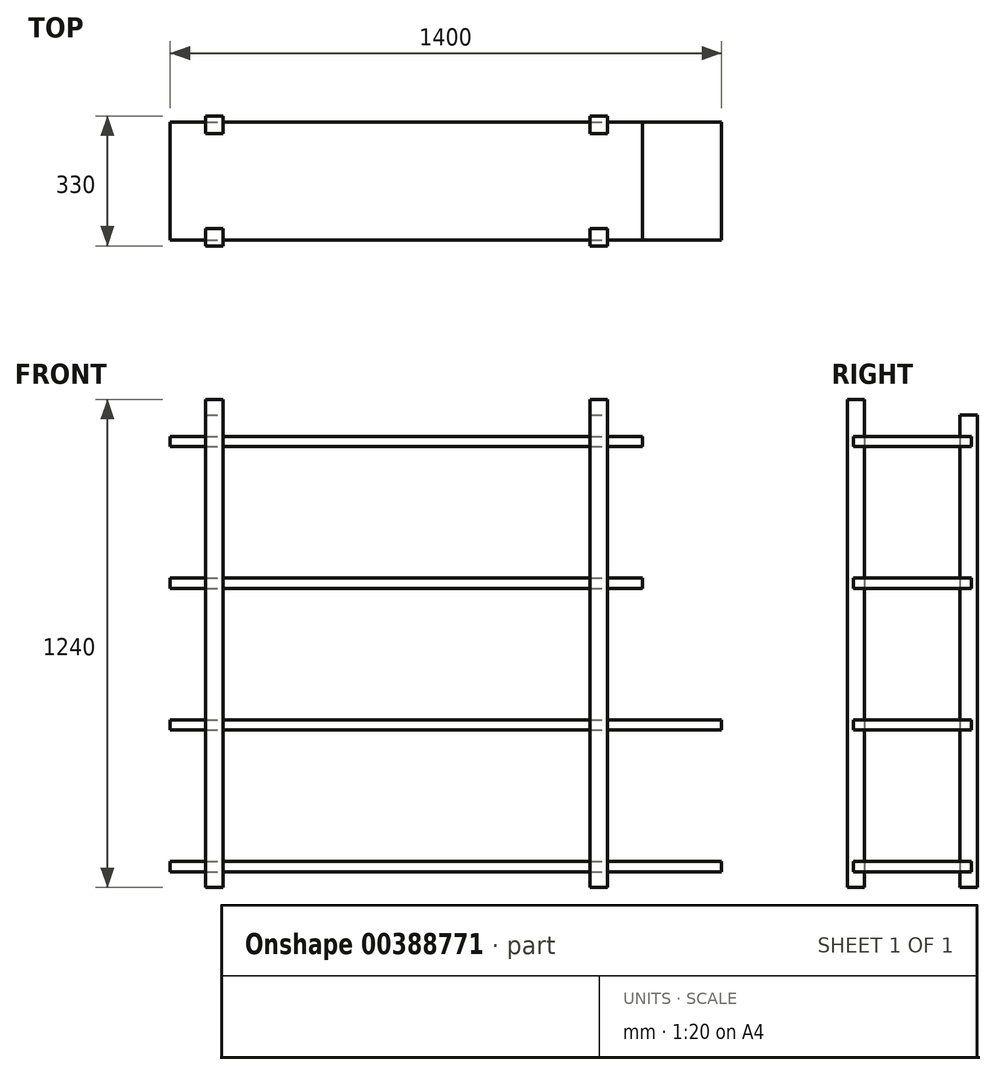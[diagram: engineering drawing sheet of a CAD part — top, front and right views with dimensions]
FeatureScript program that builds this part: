
annotation { "Feature Type Name" : "Feature", "Feature Type Description" : "" }
export const myFeature = defineFeature(function(context is Context, id is Id, definition is map)
    precondition{}
    {
        {
            var Q0;
            Q0=qCreatedBy(makeId("Front.planeOp"),FACE);
            var sketch = newSketch(context, id + "F0", { "sketchPlane" : qUnion([Q0])});
            skLineSegment(sketch, "E0.bottom", {"start": v(-700, 26) * mm, "end": v(700, 26) * mm});
            skLineSegment(sketch, "E0.top", {"start": v(-700, 0) * mm, "end": v(700, 0) * mm});
            skLineSegment(sketch, "E0.left", {"start": v(-700, 26) * mm, "end": v(-700, 0) * mm});
            skLineSegment(sketch, "E0.right", {"start": v(700, 26) * mm, "end": v(700, 0) * mm});
            skSolve(sketch);
        }
        {
            var Q0;
            Q0=qCreatedBy(makeId("Front.planeOp"),FACE);
            var sketch = newSketch(context, id + "F1", { "sketchPlane" : qUnion([Q0])});
            skLineSegment(sketch, "E1.bottom", {"start": v(-700, 386) * mm, "end": v(700, 386) * mm});
            skLineSegment(sketch, "E1.top", {"start": v(-700, 360) * mm, "end": v(700, 360) * mm});
            skLineSegment(sketch, "E1.left", {"start": v(-700, 386) * mm, "end": v(-700, 360) * mm});
            skLineSegment(sketch, "E1.right", {"start": v(700, 386) * mm, "end": v(700, 360) * mm});
            skSolve(sketch);
        }
        {
            var Q0;
            Q0=qCreatedBy(makeId("Front.planeOp"),FACE);
            var sketch = newSketch(context, id + "F2", { "sketchPlane" : qUnion([Q0])});
            skLineSegment(sketch, "E2.bottom", {"start": v(-700, 746) * mm, "end": v(500, 746) * mm});
            skLineSegment(sketch, "E2.top", {"start": v(-700, 720) * mm, "end": v(500, 720) * mm});
            skLineSegment(sketch, "E2.left", {"start": v(-700, 746) * mm, "end": v(-700, 720) * mm});
            skLineSegment(sketch, "E2.right", {"start": v(500, 746) * mm, "end": v(500, 720) * mm});
            skSolve(sketch);
        }
        {
            var Q0;
            Q0=qCreatedBy(makeId("Front.planeOp"),FACE);
            var sketch = newSketch(context, id + "F3", { "sketchPlane" : qUnion([Q0])});
            skLineSegment(sketch, "E3.bottom", {"start": v(-700, 1106) * mm, "end": v(500, 1106) * mm});
            skLineSegment(sketch, "E3.top", {"start": v(-700, 1080) * mm, "end": v(500, 1080) * mm});
            skLineSegment(sketch, "E3.left", {"start": v(-700, 1106) * mm, "end": v(-700, 1080) * mm});
            skLineSegment(sketch, "E3.right", {"start": v(500, 1106) * mm, "end": v(500, 1080) * mm});
            skSolve(sketch);
        }
        {
            var Q0;
            Q0=qCreatedBy(makeId("Front.planeOp"),FACE);
            var sketch = newSketch(context, id + "F4", { "sketchPlane" : qUnion([Q0])});
            skLineSegment(sketch, "E4.bottom", {"start": v(-610, 1160) * mm, "end": v(-566, 1160) * mm});
            skLineSegment(sketch, "E4.top", {"start": v(-610, -40) * mm, "end": v(-566, -40) * mm});
            skLineSegment(sketch, "E4.left", {"start": v(-610, 1160) * mm, "end": v(-610, -40) * mm});
            skLineSegment(sketch, "E4.right", {"start": v(-566, 1160) * mm, "end": v(-566, -40) * mm});
            skSolve(sketch);
        }
        {
            var Q0;
            Q0=qCreatedBy(makeId("Front.planeOp"),FACE);
            var sketch = newSketch(context, id + "F5", { "sketchPlane" : qUnion([Q0])});
            skLineSegment(sketch, "E5.bottom", {"start": v(366, 1160) * mm, "end": v(410, 1160) * mm});
            skLineSegment(sketch, "E5.top", {"start": v(366, -40) * mm, "end": v(410, -40) * mm});
            skLineSegment(sketch, "E5.left", {"start": v(366, 1160) * mm, "end": v(366, -40) * mm});
            skLineSegment(sketch, "E5.right", {"start": v(410, 1160) * mm, "end": v(410, -40) * mm});
            skSolve(sketch);
        }
        {
            var Q0;
            Q0=qSketchRegion(id+"F0",true);
            extrude(context, id + "F6", {"entities" : qUnion([Q0]), "depth" : 300 * mm});
        }
        {
            var Q0;
            Q0=qSketchRegion(id+"F1",true);
            var Q1;
            Q1=makeQuery(id+"F2.imprint","IMPRINT",FACE,{"disambiguationData":[TD([[makeQuery(id+"F2.imprint","IMPRINT",EDGE,{"derivedFrom":sQuery(id+"F2.wireOp",EDGE,"E2.bottom")}),-1.0]])]});
            var Q2;
            Q2=makeQuery(id+"F3.imprint","IMPRINT",FACE,{"disambiguationData":[TD([[makeQuery(id+"F3.imprint","IMPRINT",EDGE,{"derivedFrom":sQuery(id+"F3.wireOp",EDGE,"E3.bottom")}),-1.0]])]});
            extrude(context, id + "F7", {"entities" : qUnion([Q0, Q1, Q2]), "depth" : 300 * mm});
        }
        {
            var Q0;
            Q0=qCreatedBy(makeId("Top.planeOp"),FACE);
            var sketch = newSketch(context, id + "F8", { "sketchPlane" : qUnion([Q0])});
            skLineSegment(sketch, "E6.bottom", {"start": v(-610, -271) * mm, "end": v(-566, -271) * mm});
            skLineSegment(sketch, "E6.top", {"start": v(-610, -315) * mm, "end": v(-566, -315) * mm});
            skLineSegment(sketch, "E6.left", {"start": v(-610, -271) * mm, "end": v(-610, -315) * mm});
            skLineSegment(sketch, "E6.right", {"start": v(-566, -271) * mm, "end": v(-566, -315) * mm});
            skSolve(sketch);
        }
        {
            var Q0;
            Q0=qSketchRegion(id+"F8",true);
            extrude(context, id + "F9", {"entities" : qUnion([Q0]), "depth" : 1200 * mm, "hasSecondDirection" : true, "secondDirectionOppositeDirection" : true, "secondDirectionDepth" : 40 * mm});
        }
        {
            var Q0;
            Q0=qCreatedBy(makeId("Top.planeOp"),FACE);
            var sketch = newSketch(context, id + "F10", { "sketchPlane" : qUnion([Q0])});
            skLineSegment(sketch, "E7.bottom", {"start": v(366, -271) * mm, "end": v(410, -271) * mm});
            skLineSegment(sketch, "E7.top", {"start": v(366, -315) * mm, "end": v(410, -315) * mm});
            skLineSegment(sketch, "E7.left", {"start": v(366, -271) * mm, "end": v(366, -315) * mm});
            skLineSegment(sketch, "E7.right", {"start": v(410, -271) * mm, "end": v(410, -315) * mm});
            skSolve(sketch);
        }
        {
            var Q0;
            Q0=qSketchRegion(id+"F10",true);
            extrude(context, id + "F11", {"entities" : qUnion([Q0]), "depth" : 1200 * mm, "hasSecondDirection" : true, "secondDirectionOppositeDirection" : true, "secondDirectionDepth" : 40 * mm});
        }
        {
            var Q0;
            Q0=qSketchRegion(id+"F5",true);
            extrude(context, id + "F12", {"entities" : qUnion([Q0]), "depth" : 29 * mm, "hasSecondDirection" : true, "secondDirectionOppositeDirection" : true, "secondDirectionDepth" : 15 * mm});
        }
        {
            var Q0;
            Q0=qSketchRegion(id+"F4",true);
            extrude(context, id + "F13", {"entities" : qUnion([Q0]), "depth" : 29 * mm, "hasSecondDirection" : true, "secondDirectionOppositeDirection" : true, "secondDirectionDepth" : 15 * mm});
        }
    });
